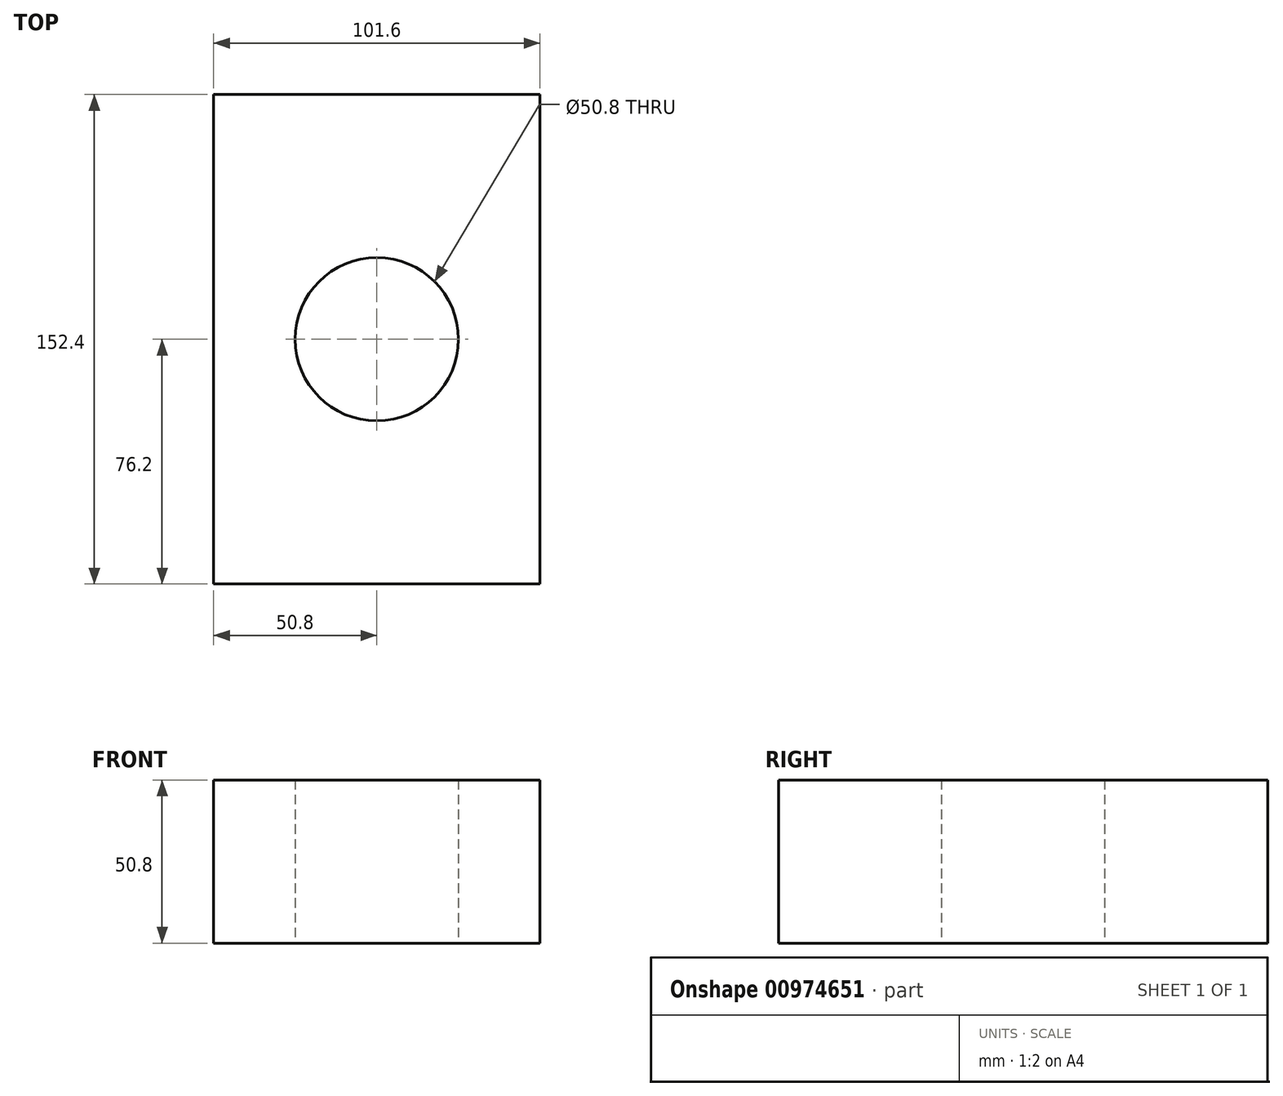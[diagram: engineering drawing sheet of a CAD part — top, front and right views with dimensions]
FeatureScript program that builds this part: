
annotation { "Feature Type Name" : "Feature", "Feature Type Description" : "" }
export const myFeature = defineFeature(function(context is Context, id is Id, definition is map)
    precondition{}
    {
        {
            var Q0;
            Q0=qCreatedBy(makeId("Top.planeOp"),FACE);
            var sketch = newSketch(context, id + "F0", { "sketchPlane" : qUnion([Q0])});
            skLineSegment(sketch, "E0.bottom", {"start": v(-50.8, 76.2) * mm, "end": v(50.8, 76.2) * mm});
            skLineSegment(sketch, "E0.top", {"start": v(-50.8, -76.2) * mm, "end": v(50.8, -76.2) * mm});
            skLineSegment(sketch, "E0.left", {"start": v(-50.8, 76.2) * mm, "end": v(-50.8, -76.2) * mm});
            skLineSegment(sketch, "E0.right", {"start": v(50.8, 76.2) * mm, "end": v(50.8, -76.2) * mm});
            skPoint(sketch, "E0.middle", {"position": v(0, 0) * mm});
            skSolve(sketch);
        }
        {
            var Q0;
            Q0=makeQuery(id+"F0.imprint","IMPRINT",FACE,{"disambiguationData":[TD([[makeQuery(id+"F0.imprint","IMPRINT",EDGE,{"derivedFrom":sQuery(id+"F0.wireOp",EDGE,"E0.bottom")}),-1.0]])]});
            var sketch = newSketch(context, id + "F1", { "sketchPlane" : qUnion([Q0])});
            skCircle(sketch, "E1", {"center": v(0, 0) * mm, "radius": 25.4 * mm});
            skSolve(sketch);
        }
        {
            var Q0;
            Q0=makeQuery(id+"F1.imprint","IMPRINT",FACE,{"disambiguationData":[TD([[makeQuery(id+"F1.imprint","IMPRINT",EDGE,{"derivedFrom":sQuery(id+"F1.wireOp",EDGE,"E1")}),-1.0]])]});
            extrude(context, id + "F2", {"entities" : qUnion([Q0]), "depth" : 50.8 * mm, "offsetDistance" : 25.4 * mm});
        }
    });
